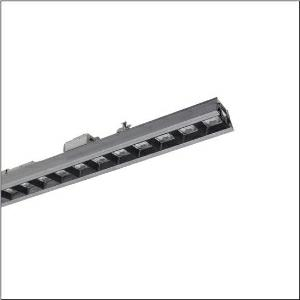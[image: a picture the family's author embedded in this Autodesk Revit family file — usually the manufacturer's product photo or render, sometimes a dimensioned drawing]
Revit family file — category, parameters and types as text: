
# Revit family: licross_r__21_silica_51ts12dn4zm00583xx_641b
name_source: partatom
category: Lighting Fixtures
units: mm (PartAtom-declared; Revit-internal decimal feet)

## family parameters
Cut with Voids When Loaded = No
Host = Face
Light Source = No
Part Type = Normal
Room Calculation Point = No
Round Connector Dimension = Use Diameter
Shared = No

## types (1)
- --- (1 x LED, 6340 lm, 39 W, 4000K)
    Apparent Load = 39 VA
    CIE Flux Codes = 86 100 100 100 100
    Color Rendering = 80
    Color Temperature = 4000K
    Default Elevation = 1800 mm
    Description = Licross® 21 Silica, luminaire insert, of sheet steel, galvanised, coil coated, silver, length: 1.500mm, width: 82mm, height: 86mm, LED rated luminous flux: 6.340lm, light colour: 840, control gear: DALI 2, with plug, 5-pole, with phase selection, mains connection: 220..240V, AC, 50/60Hz, rated input power: 39W, halogen-free wiring, primary light control with lens, of PMMA, primary anti-glare with darklight reflector, of PC, CAT 2 (L<= 1000cd/m²), light emission: direct distribution, primary light characteristic: symmetric, protection rating (complete): IP40, insulation class (complete): insulation class I (protective earthing), certification: CE, UKCA, protection symbol: D if used in an environment without relevant dust loads, impact resistance: IK03, permissible ambient temperature for indoor applications: -25..+45°C, corresponds to IFS (International Featured Standards) requirements for safety and quality in the food industry, reducing of maximum allowable ambient temperature of 5°C with ceiling mounting, LABS conformity tested according to VDMA 24364:2018-05, packaging unit: 1 piece
    Height = 86 mm
    Lamp = 1 x LED
    Lamp Light Flux = 6340 lm
    Lamp Power = 39 W
    Lamp count = 1
    Length = 1500 mm
    Luminous efficacy = 163 lm/W
    Manufacturer = Siteco
    ModVariant = No
    Model = 51TS12DN4ZM00583XX
    Mounting Place = Ceiling
    Mounting Type = Pendant
    Number of Poles = 1
    OnlyDefault = Yes
    Power Factor = 1
    Product Name = Licross® 21 Silica
    Product group = luminaire insert
    ProductGroupID = 902
    Protection Class = Protection class I
    Protection Degree = IP 40
    RLX_Detail_Level = 1
    RLX_Emergency_Light_Flux = 0 lm
    RLX_Emergency_Type = 0
    RLX_Emergency_Type_DB = No
    RlxData = <blob elided: 56881 chars, md5=9b2b2100>
    Socket = socket
    Standby Power = 0 W
    System Light Flux = 6340 lm
    System Power = 39 W
    Type Comments = factory setting: luminous flux: 100 % | dim-lin: 254 | 435 mA
    Type Image = l_1290833.jpg
    URL = http://relux.com
    VarID = @adj_106394
    Voltage = 0 V
    Weight = 0.00 kg
    Width = 82 mm  [stored 0.269029 ft]

note: [stored X ft] marks values corroborated as IEEE doubles in the binary element streams (Revit-internal decimal feet)

## geometry (parser evidence)
native form markers: Blend x4, Sweep x10
no freeform markers — native parametric forms only
